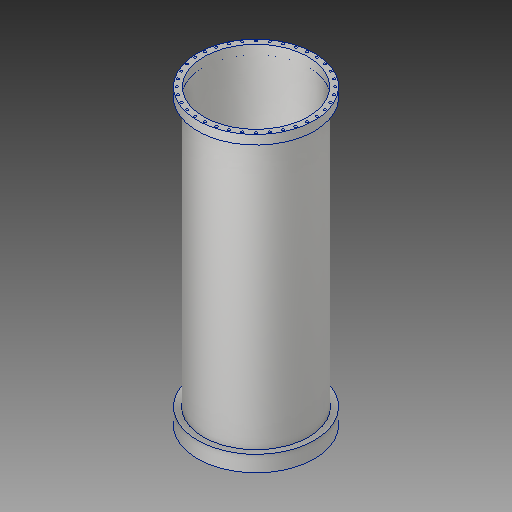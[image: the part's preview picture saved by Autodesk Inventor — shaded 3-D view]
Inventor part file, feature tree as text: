
AUTODESK INVENTOR PART (.ipt)
format: ipt  version: 2018 (Build 220112000, 112)  size: 178,176 bytes
history: native  units: in
note: dims shown in document units (in); Inventor stores cm internally (conversion verified against a paired STEP export)
features: sketch x5, extrude x4, hole x1, pattern_circular x1
ambient origin geometry x8: Origin, YZ Plane, XZ Plane, XY Plane, X Axis, Y Axis, Z Axis, Center Point
bodies: Solid1 (feature_tree)
feature tree (11):
  extrude  "Extrusion1"  Depth=11.375in
  extrude  "Extrusion2"  Depth=1.0in
  extrude  "Extrusion3"  Depth=29.25in TaperAngle=0.0deg
  extrude  "Extrusion4"  Depth=12.75in
  hole  "Hole1"  [1 undecoded]
  pattern_circular  "Circular Pattern1"  [2 undecoded]
  sketch  "Sketch1"  dims[d0=12.75in d1=11.375in]
  sketch  "Sketch2"  dims[d2=1.0in d3=0.0in d4=11.375in]
  sketch  "Sketch3"  dims[d5=11.5in d6=29.25in d7=0.0in]
  sketch  "Sketch4"  dims[d8=11.375in d9=12.75in]
  sketch  "Sketch5"  dims[d10=1.0in d11=0.0in d12=12.75in d13=0.75in d14=0.0in d15=6.125in d16=0.0344in d17=0.266in d18=0.472in d19=0.375in d20=0.25in d21=0.5635in d22=0.673in d23=0.8108in d24=14.1732in d25=360.0deg]
note: 3 required parameter values undecoded (feature->parameter linkage not recoverable at this tier; creation-order binding heuristic only, values carry confidence <= 0.55)
